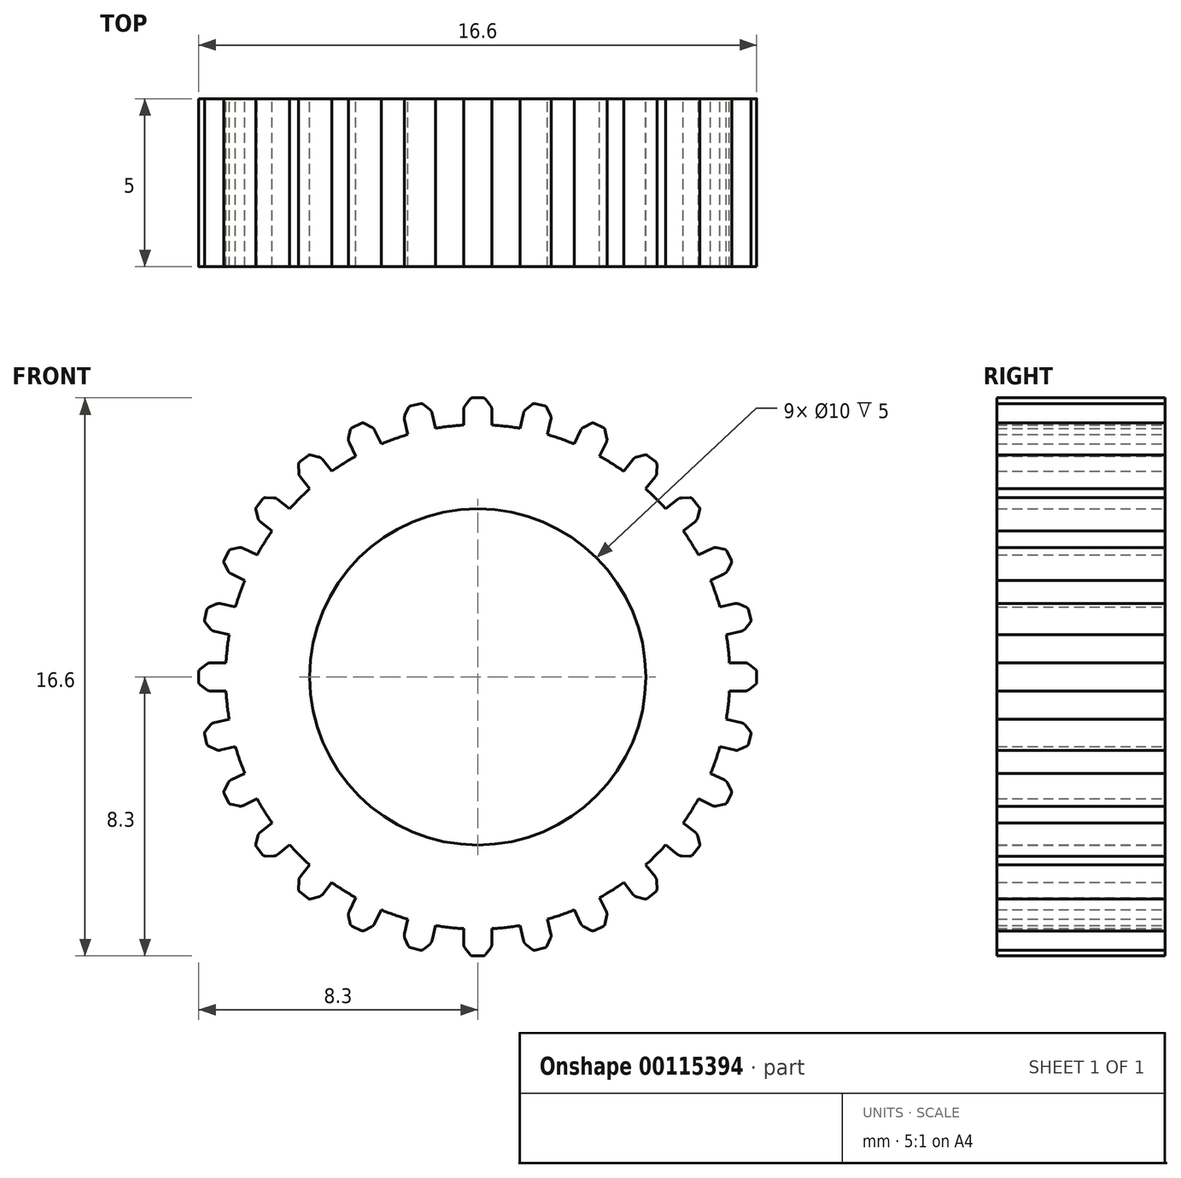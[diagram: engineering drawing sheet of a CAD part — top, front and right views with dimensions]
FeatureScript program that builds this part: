
annotation { "Feature Type Name" : "Feature", "Feature Type Description" : "" }
export const myFeature = defineFeature(function(context is Context, id is Id, definition is map)
    precondition{}
    {
        {
            var Q0;
            Q0=qCreatedBy(makeId("Front.planeOp"),FACE);
            var sketch = newSketch(context, id + "F0", { "sketchPlane" : qUnion([Q0])});
            skCircle(sketch, "E0", {"center": v(0, 0) * mm, "radius": 7.5 * mm});
            skLineSegment(sketch, "E1.bottom", {"start": v(0, 8.3) * mm, "end": v(-0.15, 8.3) * mm});
            skLineSegment(sketch, "E1.left", {"start": v(0, 8.3) * mm, "end": v(0, 7.5) * mm});
            skLineSegment(sketch, "E2.right", {"start": v(-0.42, 7.94) * mm, "end": v(-0.42, 7.49) * mm});
            skLineSegment(sketch, "E3", {"start": v(-0.38, 8.07) * mm, "end": v(-0.23, 8.26) * mm});
            skPoint(sketch, "E4.visualSharp", {"position": v(-0.2, 8.3) * mm});
            skArc(sketch, "E4.filletArc", {"start": v(-0.15, 8.3) * mm, "mid": v(-0.2, 8.29) * mm, "end": v(-0.23, 8.26) * mm});
            skPoint(sketch, "E5.visualSharp", {"position": v(-0.42, 8.01) * mm});
            skArc(sketch, "E5.filletArc", {"start": v(-0.38, 8.07) * mm, "mid": v(-0.4, 8) * mm, "end": v(-0.42, 7.94) * mm});
            skArc(sketch, "E6.MirrorCS", {"start": v(0.15, 8.3) * mm, "mid": v(0.2, 8.29) * mm, "end": v(0.23, 8.26) * mm});
            skArc(sketch, "E7.MirrorCS", {"start": v(0.38, 8.07) * mm, "mid": v(0.4, 8) * mm, "end": v(0.42, 7.94) * mm});
            skLineSegment(sketch, "E8.MirrorCS", {"start": v(0, 8.3) * mm, "end": v(0.15, 8.3) * mm});
            skPoint(sketch, "E9.MirrorP", {"position": v(0.2, 8.3) * mm});
            skLineSegment(sketch, "E10.MirrorCS", {"start": v(0.38, 8.07) * mm, "end": v(0.23, 8.26) * mm});
            skPoint(sketch, "E11.MirrorP", {"position": v(0.42, 8.01) * mm});
            skLineSegment(sketch, "E12.MirrorCS", {"start": v(0.42, 7.94) * mm, "end": v(0.42, 7.49) * mm});
            skPoint(sketch, "E13.1.0", {"position": v(-2.2, 7.72) * mm});
            skPoint(sketch, "E13.1.1", {"position": v(-1.65, 8.14) * mm});
            skPoint(sketch, "E13.1.2", {"position": v(-1.37, 7.9) * mm});
            skPoint(sketch, "E13.1.3", {"position": v(-2.04, 8.05) * mm});
            skArc(sketch, "E13.1.4", {"start": v(-2.16, 7.78) * mm, "mid": v(-2.18, 7.72) * mm, "end": v(-2.18, 7.65) * mm});
            skLineSegment(sketch, "E13.1.5", {"start": v(-1.43, 7.95) * mm, "end": v(-1.61, 8.1) * mm});
            skArc(sketch, "E13.1.6", {"start": v(-1.43, 7.95) * mm, "mid": v(-1.38, 7.9) * mm, "end": v(-1.36, 7.84) * mm});
            skLineSegment(sketch, "E13.1.7", {"start": v(-2.16, 7.78) * mm, "end": v(-2.06, 8) * mm});
            skArc(sketch, "E13.1.8", {"start": v(-1.7, 8.13) * mm, "mid": v(-1.66, 8.13) * mm, "end": v(-1.61, 8.1) * mm});
            skArc(sketch, "E13.1.9", {"start": v(-2, 8.06) * mm, "mid": v(-2.03, 8.04) * mm, "end": v(-2.06, 8) * mm});
            skLineSegment(sketch, "E13.1.10", {"start": v(-1.85, 8.1) * mm, "end": v(-1.7, 8.13) * mm});
            skLineSegment(sketch, "E13.1.11", {"start": v(-1.85, 8.1) * mm, "end": v(-2, 8.06) * mm});
            skLineSegment(sketch, "E13.1.12", {"start": v(-2.18, 7.65) * mm, "end": v(-2.08, 7.2) * mm});
            skLineSegment(sketch, "E13.1.13", {"start": v(-1.36, 7.84) * mm, "end": v(-1.26, 7.4) * mm});
            skPoint(sketch, "E13.2.0", {"position": v(-3.85, 7.04) * mm});
            skPoint(sketch, "E13.2.1", {"position": v(-3.42, 7.56) * mm});
            skPoint(sketch, "E13.2.2", {"position": v(-3.1, 7.4) * mm});
            skPoint(sketch, "E13.2.3", {"position": v(-3.78, 7.4) * mm});
            skArc(sketch, "E13.2.4", {"start": v(-3.84, 7.1) * mm, "mid": v(-3.84, 7.04) * mm, "end": v(-3.83, 6.97) * mm});
            skLineSegment(sketch, "E13.2.5", {"start": v(-3.16, 7.43) * mm, "end": v(-3.38, 7.54) * mm});
            skArc(sketch, "E13.2.6", {"start": v(-3.16, 7.43) * mm, "mid": v(-3.1, 7.4) * mm, "end": v(-3.07, 7.34) * mm});
            skLineSegment(sketch, "E13.2.7", {"start": v(-3.84, 7.1) * mm, "end": v(-3.8, 7.34) * mm});
            skArc(sketch, "E13.2.8", {"start": v(-3.47, 7.54) * mm, "mid": v(-3.42, 7.55) * mm, "end": v(-3.38, 7.54) * mm});
            skArc(sketch, "E13.2.9", {"start": v(-3.74, 7.41) * mm, "mid": v(-3.77, 7.38) * mm, "end": v(-3.8, 7.34) * mm});
            skLineSegment(sketch, "E13.2.10", {"start": v(-3.6, 7.48) * mm, "end": v(-3.47, 7.54) * mm});
            skLineSegment(sketch, "E13.2.11", {"start": v(-3.6, 7.48) * mm, "end": v(-3.74, 7.41) * mm});
            skLineSegment(sketch, "E13.2.12", {"start": v(-3.83, 6.97) * mm, "end": v(-3.63, 6.56) * mm});
            skLineSegment(sketch, "E13.2.13", {"start": v(-3.07, 7.34) * mm, "end": v(-2.87, 6.93) * mm});
            skPoint(sketch, "E13.3.0", {"position": v(-5.32, 6) * mm});
            skPoint(sketch, "E13.3.1", {"position": v(-5.02, 6.61) * mm});
            skPoint(sketch, "E13.3.2", {"position": v(-4.67, 6.53) * mm});
            skPoint(sketch, "E13.3.3", {"position": v(-5.33, 6.36) * mm});
            skArc(sketch, "E13.3.4", {"start": v(-5.33, 6.07) * mm, "mid": v(-5.31, 6) * mm, "end": v(-5.28, 5.95) * mm});
            skLineSegment(sketch, "E13.3.5", {"start": v(-4.73, 6.54) * mm, "end": v(-4.97, 6.6) * mm});
            skArc(sketch, "E13.3.6", {"start": v(-4.73, 6.54) * mm, "mid": v(-4.67, 6.52) * mm, "end": v(-4.62, 6.47) * mm});
            skLineSegment(sketch, "E13.3.7", {"start": v(-5.33, 6.07) * mm, "end": v(-5.33, 6.32) * mm});
            skArc(sketch, "E13.3.8", {"start": v(-5.06, 6.58) * mm, "mid": v(-5.02, 6.6) * mm, "end": v(-4.97, 6.6) * mm});
            skArc(sketch, "E13.3.9", {"start": v(-5.3, 6.4) * mm, "mid": v(-5.32, 6.36) * mm, "end": v(-5.33, 6.32) * mm});
            skLineSegment(sketch, "E13.3.10", {"start": v(-5.17, 6.49) * mm, "end": v(-5.06, 6.58) * mm});
            skLineSegment(sketch, "E13.3.11", {"start": v(-5.17, 6.49) * mm, "end": v(-5.3, 6.4) * mm});
            skLineSegment(sketch, "E13.3.12", {"start": v(-5.28, 5.95) * mm, "end": v(-5, 5.6) * mm});
            skLineSegment(sketch, "E13.3.13", {"start": v(-4.62, 6.47) * mm, "end": v(-4.34, 6.12) * mm});
            skPoint(sketch, "E13.4.0", {"position": v(-6.53, 4.67) * mm});
            skPoint(sketch, "E13.4.1", {"position": v(-6.36, 5.33) * mm});
            skPoint(sketch, "E13.4.2", {"position": v(-6, 5.32) * mm});
            skPoint(sketch, "E13.4.3", {"position": v(-6.61, 5.02) * mm});
            skArc(sketch, "E13.4.4", {"start": v(-6.54, 4.73) * mm, "mid": v(-6.52, 4.67) * mm, "end": v(-6.47, 4.62) * mm});
            skLineSegment(sketch, "E13.4.5", {"start": v(-6.07, 5.33) * mm, "end": v(-6.32, 5.33) * mm});
            skArc(sketch, "E13.4.6", {"start": v(-6.07, 5.33) * mm, "mid": v(-6, 5.31) * mm, "end": v(-5.95, 5.28) * mm});
            skLineSegment(sketch, "E13.4.7", {"start": v(-6.54, 4.73) * mm, "end": v(-6.6, 4.97) * mm});
            skArc(sketch, "E13.4.8", {"start": v(-6.4, 5.3) * mm, "mid": v(-6.36, 5.32) * mm, "end": v(-6.32, 5.33) * mm});
            skArc(sketch, "E13.4.9", {"start": v(-6.58, 5.06) * mm, "mid": v(-6.6, 5.02) * mm, "end": v(-6.6, 4.97) * mm});
            skLineSegment(sketch, "E13.4.10", {"start": v(-6.49, 5.17) * mm, "end": v(-6.4, 5.3) * mm});
            skLineSegment(sketch, "E13.4.11", {"start": v(-6.49, 5.17) * mm, "end": v(-6.58, 5.06) * mm});
            skLineSegment(sketch, "E13.4.12", {"start": v(-6.47, 4.62) * mm, "end": v(-6.12, 4.34) * mm});
            skLineSegment(sketch, "E13.4.13", {"start": v(-5.95, 5.28) * mm, "end": v(-5.6, 5) * mm});
            skPoint(sketch, "E13.5.0", {"position": v(-7.4, 3.1) * mm});
            skPoint(sketch, "E13.5.1", {"position": v(-7.4, 3.78) * mm});
            skPoint(sketch, "E13.5.2", {"position": v(-7.04, 3.85) * mm});
            skPoint(sketch, "E13.5.3", {"position": v(-7.56, 3.42) * mm});
            skArc(sketch, "E13.5.4", {"start": v(-7.43, 3.16) * mm, "mid": v(-7.4, 3.1) * mm, "end": v(-7.34, 3.07) * mm});
            skLineSegment(sketch, "E13.5.5", {"start": v(-7.1, 3.84) * mm, "end": v(-7.34, 3.8) * mm});
            skArc(sketch, "E13.5.6", {"start": v(-7.1, 3.84) * mm, "mid": v(-7.04, 3.84) * mm, "end": v(-6.97, 3.83) * mm});
            skLineSegment(sketch, "E13.5.7", {"start": v(-7.43, 3.16) * mm, "end": v(-7.54, 3.38) * mm});
            skArc(sketch, "E13.5.8", {"start": v(-7.41, 3.74) * mm, "mid": v(-7.38, 3.77) * mm, "end": v(-7.34, 3.8) * mm});
            skArc(sketch, "E13.5.9", {"start": v(-7.54, 3.47) * mm, "mid": v(-7.55, 3.42) * mm, "end": v(-7.54, 3.38) * mm});
            skLineSegment(sketch, "E13.5.10", {"start": v(-7.48, 3.6) * mm, "end": v(-7.41, 3.74) * mm});
            skLineSegment(sketch, "E13.5.11", {"start": v(-7.48, 3.6) * mm, "end": v(-7.54, 3.47) * mm});
            skLineSegment(sketch, "E13.5.12", {"start": v(-7.34, 3.07) * mm, "end": v(-6.93, 2.87) * mm});
            skLineSegment(sketch, "E13.5.13", {"start": v(-6.97, 3.83) * mm, "end": v(-6.56, 3.63) * mm});
            skPoint(sketch, "E13.6.0", {"position": v(-7.9, 1.37) * mm});
            skPoint(sketch, "E13.6.1", {"position": v(-8.05, 2.04) * mm});
            skPoint(sketch, "E13.6.2", {"position": v(-7.72, 2.2) * mm});
            skPoint(sketch, "E13.6.3", {"position": v(-8.14, 1.65) * mm});
            skArc(sketch, "E13.6.4", {"start": v(-7.95, 1.43) * mm, "mid": v(-7.9, 1.38) * mm, "end": v(-7.84, 1.36) * mm});
            skLineSegment(sketch, "E13.6.5", {"start": v(-7.78, 2.16) * mm, "end": v(-8, 2.06) * mm});
            skArc(sketch, "E13.6.6", {"start": v(-7.78, 2.16) * mm, "mid": v(-7.72, 2.18) * mm, "end": v(-7.65, 2.18) * mm});
            skLineSegment(sketch, "E13.6.7", {"start": v(-7.95, 1.43) * mm, "end": v(-8.1, 1.61) * mm});
            skArc(sketch, "E13.6.8", {"start": v(-8.06, 2) * mm, "mid": v(-8.04, 2.03) * mm, "end": v(-8, 2.06) * mm});
            skArc(sketch, "E13.6.9", {"start": v(-8.13, 1.7) * mm, "mid": v(-8.13, 1.66) * mm, "end": v(-8.1, 1.61) * mm});
            skLineSegment(sketch, "E13.6.10", {"start": v(-8.1, 1.85) * mm, "end": v(-8.06, 2) * mm});
            skLineSegment(sketch, "E13.6.11", {"start": v(-8.1, 1.85) * mm, "end": v(-8.13, 1.7) * mm});
            skLineSegment(sketch, "E13.6.12", {"start": v(-7.84, 1.36) * mm, "end": v(-7.4, 1.26) * mm});
            skLineSegment(sketch, "E13.6.13", {"start": v(-7.65, 2.18) * mm, "end": v(-7.2, 2.08) * mm});
            skPoint(sketch, "E13.7.0", {"position": v(-8.01, -0.42) * mm});
            skPoint(sketch, "E13.7.1", {"position": v(-8.3, 0.2) * mm});
            skPoint(sketch, "E13.7.2", {"position": v(-8.01, 0.42) * mm});
            skPoint(sketch, "E13.7.3", {"position": v(-8.3, -0.2) * mm});
            skArc(sketch, "E13.7.4", {"start": v(-8.07, -0.38) * mm, "mid": v(-8, -0.4) * mm, "end": v(-7.94, -0.42) * mm});
            skLineSegment(sketch, "E13.7.5", {"start": v(-8.07, 0.38) * mm, "end": v(-8.26, 0.23) * mm});
            skArc(sketch, "E13.7.6", {"start": v(-8.07, 0.38) * mm, "mid": v(-8, 0.4) * mm, "end": v(-7.94, 0.42) * mm});
            skLineSegment(sketch, "E13.7.7", {"start": v(-8.07, -0.38) * mm, "end": v(-8.26, -0.23) * mm});
            skArc(sketch, "E13.7.8", {"start": v(-8.3, 0.15) * mm, "mid": v(-8.29, 0.2) * mm, "end": v(-8.26, 0.23) * mm});
            skArc(sketch, "E13.7.9", {"start": v(-8.3, -0.15) * mm, "mid": v(-8.29, -0.2) * mm, "end": v(-8.26, -0.23) * mm});
            skLineSegment(sketch, "E13.7.10", {"start": v(-8.3, 0) * mm, "end": v(-8.3, 0.15) * mm});
            skLineSegment(sketch, "E13.7.11", {"start": v(-8.3, 0) * mm, "end": v(-8.3, -0.15) * mm});
            skLineSegment(sketch, "E13.7.12", {"start": v(-7.94, -0.42) * mm, "end": v(-7.49, -0.42) * mm});
            skLineSegment(sketch, "E13.7.13", {"start": v(-7.94, 0.42) * mm, "end": v(-7.49, 0.42) * mm});
            skPoint(sketch, "E13.8.0", {"position": v(-7.72, -2.2) * mm});
            skPoint(sketch, "E13.8.1", {"position": v(-8.14, -1.65) * mm});
            skPoint(sketch, "E13.8.2", {"position": v(-7.9, -1.37) * mm});
            skPoint(sketch, "E13.8.3", {"position": v(-8.05, -2.04) * mm});
            skArc(sketch, "E13.8.4", {"start": v(-7.78, -2.16) * mm, "mid": v(-7.72, -2.18) * mm, "end": v(-7.65, -2.18) * mm});
            skLineSegment(sketch, "E13.8.5", {"start": v(-7.95, -1.43) * mm, "end": v(-8.1, -1.61) * mm});
            skArc(sketch, "E13.8.6", {"start": v(-7.95, -1.43) * mm, "mid": v(-7.9, -1.38) * mm, "end": v(-7.84, -1.36) * mm});
            skLineSegment(sketch, "E13.8.7", {"start": v(-7.78, -2.16) * mm, "end": v(-8, -2.06) * mm});
            skArc(sketch, "E13.8.8", {"start": v(-8.13, -1.7) * mm, "mid": v(-8.13, -1.66) * mm, "end": v(-8.1, -1.61) * mm});
            skArc(sketch, "E13.8.9", {"start": v(-8.06, -2) * mm, "mid": v(-8.04, -2.03) * mm, "end": v(-8, -2.06) * mm});
            skLineSegment(sketch, "E13.8.10", {"start": v(-8.1, -1.85) * mm, "end": v(-8.13, -1.7) * mm});
            skLineSegment(sketch, "E13.8.11", {"start": v(-8.1, -1.85) * mm, "end": v(-8.06, -2) * mm});
            skLineSegment(sketch, "E13.8.12", {"start": v(-7.65, -2.18) * mm, "end": v(-7.2, -2.08) * mm});
            skLineSegment(sketch, "E13.8.13", {"start": v(-7.84, -1.36) * mm, "end": v(-7.4, -1.26) * mm});
            skPoint(sketch, "E13.9.0", {"position": v(-7.04, -3.85) * mm});
            skPoint(sketch, "E13.9.1", {"position": v(-7.56, -3.42) * mm});
            skPoint(sketch, "E13.9.2", {"position": v(-7.4, -3.1) * mm});
            skPoint(sketch, "E13.9.3", {"position": v(-7.4, -3.78) * mm});
            skArc(sketch, "E13.9.4", {"start": v(-7.1, -3.84) * mm, "mid": v(-7.04, -3.84) * mm, "end": v(-6.97, -3.83) * mm});
            skLineSegment(sketch, "E13.9.5", {"start": v(-7.43, -3.16) * mm, "end": v(-7.54, -3.38) * mm});
            skArc(sketch, "E13.9.6", {"start": v(-7.43, -3.16) * mm, "mid": v(-7.4, -3.1) * mm, "end": v(-7.34, -3.07) * mm});
            skLineSegment(sketch, "E13.9.7", {"start": v(-7.1, -3.84) * mm, "end": v(-7.34, -3.8) * mm});
            skArc(sketch, "E13.9.8", {"start": v(-7.54, -3.47) * mm, "mid": v(-7.55, -3.42) * mm, "end": v(-7.54, -3.38) * mm});
            skArc(sketch, "E13.9.9", {"start": v(-7.41, -3.74) * mm, "mid": v(-7.38, -3.77) * mm, "end": v(-7.34, -3.8) * mm});
            skLineSegment(sketch, "E13.9.10", {"start": v(-7.48, -3.6) * mm, "end": v(-7.54, -3.47) * mm});
            skLineSegment(sketch, "E13.9.11", {"start": v(-7.48, -3.6) * mm, "end": v(-7.41, -3.74) * mm});
            skLineSegment(sketch, "E13.9.12", {"start": v(-6.97, -3.83) * mm, "end": v(-6.56, -3.63) * mm});
            skLineSegment(sketch, "E13.9.13", {"start": v(-7.34, -3.07) * mm, "end": v(-6.93, -2.87) * mm});
            skPoint(sketch, "E13.10.0", {"position": v(-6, -5.32) * mm});
            skPoint(sketch, "E13.10.1", {"position": v(-6.61, -5.02) * mm});
            skPoint(sketch, "E13.10.2", {"position": v(-6.53, -4.67) * mm});
            skPoint(sketch, "E13.10.3", {"position": v(-6.36, -5.33) * mm});
            skArc(sketch, "E13.10.4", {"start": v(-6.07, -5.33) * mm, "mid": v(-6, -5.31) * mm, "end": v(-5.95, -5.28) * mm});
            skLineSegment(sketch, "E13.10.5", {"start": v(-6.54, -4.73) * mm, "end": v(-6.6, -4.97) * mm});
            skArc(sketch, "E13.10.6", {"start": v(-6.54, -4.73) * mm, "mid": v(-6.52, -4.67) * mm, "end": v(-6.47, -4.62) * mm});
            skLineSegment(sketch, "E13.10.7", {"start": v(-6.07, -5.33) * mm, "end": v(-6.32, -5.33) * mm});
            skArc(sketch, "E13.10.8", {"start": v(-6.58, -5.06) * mm, "mid": v(-6.6, -5.02) * mm, "end": v(-6.6, -4.97) * mm});
            skArc(sketch, "E13.10.9", {"start": v(-6.4, -5.3) * mm, "mid": v(-6.36, -5.32) * mm, "end": v(-6.32, -5.33) * mm});
            skLineSegment(sketch, "E13.10.10", {"start": v(-6.49, -5.17) * mm, "end": v(-6.58, -5.06) * mm});
            skLineSegment(sketch, "E13.10.11", {"start": v(-6.49, -5.17) * mm, "end": v(-6.4, -5.3) * mm});
            skLineSegment(sketch, "E13.10.12", {"start": v(-5.95, -5.28) * mm, "end": v(-5.6, -5) * mm});
            skLineSegment(sketch, "E13.10.13", {"start": v(-6.47, -4.62) * mm, "end": v(-6.12, -4.34) * mm});
            skPoint(sketch, "E13.11.0", {"position": v(-4.67, -6.53) * mm});
            skPoint(sketch, "E13.11.1", {"position": v(-5.33, -6.36) * mm});
            skPoint(sketch, "E13.11.2", {"position": v(-5.32, -6) * mm});
            skPoint(sketch, "E13.11.3", {"position": v(-5.02, -6.61) * mm});
            skArc(sketch, "E13.11.4", {"start": v(-4.73, -6.54) * mm, "mid": v(-4.67, -6.52) * mm, "end": v(-4.62, -6.47) * mm});
            skLineSegment(sketch, "E13.11.5", {"start": v(-5.33, -6.07) * mm, "end": v(-5.33, -6.32) * mm});
            skArc(sketch, "E13.11.6", {"start": v(-5.33, -6.07) * mm, "mid": v(-5.31, -6) * mm, "end": v(-5.28, -5.95) * mm});
            skLineSegment(sketch, "E13.11.7", {"start": v(-4.73, -6.54) * mm, "end": v(-4.97, -6.6) * mm});
            skArc(sketch, "E13.11.8", {"start": v(-5.3, -6.4) * mm, "mid": v(-5.32, -6.36) * mm, "end": v(-5.33, -6.32) * mm});
            skArc(sketch, "E13.11.9", {"start": v(-5.06, -6.58) * mm, "mid": v(-5.02, -6.6) * mm, "end": v(-4.97, -6.6) * mm});
            skLineSegment(sketch, "E13.11.10", {"start": v(-5.17, -6.49) * mm, "end": v(-5.3, -6.4) * mm});
            skLineSegment(sketch, "E13.11.11", {"start": v(-5.17, -6.49) * mm, "end": v(-5.06, -6.58) * mm});
            skLineSegment(sketch, "E13.11.12", {"start": v(-4.62, -6.47) * mm, "end": v(-4.34, -6.12) * mm});
            skLineSegment(sketch, "E13.11.13", {"start": v(-5.28, -5.95) * mm, "end": v(-5, -5.6) * mm});
            skPoint(sketch, "E13.12.0", {"position": v(-3.1, -7.4) * mm});
            skPoint(sketch, "E13.12.1", {"position": v(-3.78, -7.4) * mm});
            skPoint(sketch, "E13.12.2", {"position": v(-3.85, -7.04) * mm});
            skPoint(sketch, "E13.12.3", {"position": v(-3.42, -7.56) * mm});
            skArc(sketch, "E13.12.4", {"start": v(-3.16, -7.43) * mm, "mid": v(-3.1, -7.4) * mm, "end": v(-3.07, -7.34) * mm});
            skLineSegment(sketch, "E13.12.5", {"start": v(-3.84, -7.1) * mm, "end": v(-3.8, -7.34) * mm});
            skArc(sketch, "E13.12.6", {"start": v(-3.84, -7.1) * mm, "mid": v(-3.84, -7.04) * mm, "end": v(-3.83, -6.97) * mm});
            skLineSegment(sketch, "E13.12.7", {"start": v(-3.16, -7.43) * mm, "end": v(-3.38, -7.54) * mm});
            skArc(sketch, "E13.12.8", {"start": v(-3.74, -7.41) * mm, "mid": v(-3.77, -7.38) * mm, "end": v(-3.8, -7.34) * mm});
            skArc(sketch, "E13.12.9", {"start": v(-3.47, -7.54) * mm, "mid": v(-3.42, -7.55) * mm, "end": v(-3.38, -7.54) * mm});
            skLineSegment(sketch, "E13.12.10", {"start": v(-3.6, -7.48) * mm, "end": v(-3.74, -7.41) * mm});
            skLineSegment(sketch, "E13.12.11", {"start": v(-3.6, -7.48) * mm, "end": v(-3.47, -7.54) * mm});
            skLineSegment(sketch, "E13.12.12", {"start": v(-3.07, -7.34) * mm, "end": v(-2.87, -6.93) * mm});
            skLineSegment(sketch, "E13.12.13", {"start": v(-3.83, -6.97) * mm, "end": v(-3.63, -6.56) * mm});
            skPoint(sketch, "E13.13.0", {"position": v(-1.37, -7.9) * mm});
            skPoint(sketch, "E13.13.1", {"position": v(-2.04, -8.05) * mm});
            skPoint(sketch, "E13.13.2", {"position": v(-2.2, -7.72) * mm});
            skPoint(sketch, "E13.13.3", {"position": v(-1.65, -8.14) * mm});
            skArc(sketch, "E13.13.4", {"start": v(-1.43, -7.95) * mm, "mid": v(-1.38, -7.9) * mm, "end": v(-1.36, -7.84) * mm});
            skLineSegment(sketch, "E13.13.5", {"start": v(-2.16, -7.78) * mm, "end": v(-2.06, -8) * mm});
            skArc(sketch, "E13.13.6", {"start": v(-2.16, -7.78) * mm, "mid": v(-2.18, -7.72) * mm, "end": v(-2.18, -7.65) * mm});
            skLineSegment(sketch, "E13.13.7", {"start": v(-1.43, -7.95) * mm, "end": v(-1.61, -8.1) * mm});
            skArc(sketch, "E13.13.8", {"start": v(-2, -8.06) * mm, "mid": v(-2.03, -8.04) * mm, "end": v(-2.06, -8) * mm});
            skArc(sketch, "E13.13.9", {"start": v(-1.7, -8.13) * mm, "mid": v(-1.66, -8.13) * mm, "end": v(-1.61, -8.1) * mm});
            skLineSegment(sketch, "E13.13.10", {"start": v(-1.85, -8.1) * mm, "end": v(-2, -8.06) * mm});
            skLineSegment(sketch, "E13.13.11", {"start": v(-1.85, -8.1) * mm, "end": v(-1.7, -8.13) * mm});
            skLineSegment(sketch, "E13.13.12", {"start": v(-1.36, -7.84) * mm, "end": v(-1.26, -7.4) * mm});
            skLineSegment(sketch, "E13.13.13", {"start": v(-2.18, -7.65) * mm, "end": v(-2.08, -7.2) * mm});
            skPoint(sketch, "E13.14.0", {"position": v(0.42, -8.01) * mm});
            skPoint(sketch, "E13.14.1", {"position": v(-0.2, -8.3) * mm});
            skPoint(sketch, "E13.14.2", {"position": v(-0.42, -8.01) * mm});
            skPoint(sketch, "E13.14.3", {"position": v(0.2, -8.3) * mm});
            skArc(sketch, "E13.14.4", {"start": v(0.38, -8.07) * mm, "mid": v(0.4, -8) * mm, "end": v(0.42, -7.94) * mm});
            skLineSegment(sketch, "E13.14.5", {"start": v(-0.38, -8.07) * mm, "end": v(-0.23, -8.26) * mm});
            skArc(sketch, "E13.14.6", {"start": v(-0.38, -8.07) * mm, "mid": v(-0.4, -8) * mm, "end": v(-0.42, -7.94) * mm});
            skLineSegment(sketch, "E13.14.7", {"start": v(0.38, -8.07) * mm, "end": v(0.23, -8.26) * mm});
            skArc(sketch, "E13.14.8", {"start": v(-0.15, -8.3) * mm, "mid": v(-0.2, -8.29) * mm, "end": v(-0.23, -8.26) * mm});
            skArc(sketch, "E13.14.9", {"start": v(0.15, -8.3) * mm, "mid": v(0.2, -8.29) * mm, "end": v(0.23, -8.26) * mm});
            skLineSegment(sketch, "E13.14.10", {"start": v(0, -8.3) * mm, "end": v(-0.15, -8.3) * mm});
            skLineSegment(sketch, "E13.14.11", {"start": v(0, -8.3) * mm, "end": v(0.15, -8.3) * mm});
            skLineSegment(sketch, "E13.14.12", {"start": v(0.42, -7.94) * mm, "end": v(0.42, -7.49) * mm});
            skLineSegment(sketch, "E13.14.13", {"start": v(-0.42, -7.94) * mm, "end": v(-0.42, -7.49) * mm});
            skPoint(sketch, "E13.15.0", {"position": v(2.2, -7.72) * mm});
            skPoint(sketch, "E13.15.1", {"position": v(1.65, -8.14) * mm});
            skPoint(sketch, "E13.15.2", {"position": v(1.37, -7.9) * mm});
            skPoint(sketch, "E13.15.3", {"position": v(2.04, -8.05) * mm});
            skArc(sketch, "E13.15.4", {"start": v(2.16, -7.78) * mm, "mid": v(2.18, -7.72) * mm, "end": v(2.18, -7.65) * mm});
            skLineSegment(sketch, "E13.15.5", {"start": v(1.43, -7.95) * mm, "end": v(1.61, -8.1) * mm});
            skArc(sketch, "E13.15.6", {"start": v(1.43, -7.95) * mm, "mid": v(1.38, -7.9) * mm, "end": v(1.36, -7.84) * mm});
            skLineSegment(sketch, "E13.15.7", {"start": v(2.16, -7.78) * mm, "end": v(2.06, -8) * mm});
            skArc(sketch, "E13.15.8", {"start": v(1.7, -8.13) * mm, "mid": v(1.66, -8.13) * mm, "end": v(1.61, -8.1) * mm});
            skArc(sketch, "E13.15.9", {"start": v(2, -8.06) * mm, "mid": v(2.03, -8.04) * mm, "end": v(2.06, -8) * mm});
            skLineSegment(sketch, "E13.15.10", {"start": v(1.85, -8.1) * mm, "end": v(1.7, -8.13) * mm});
            skLineSegment(sketch, "E13.15.11", {"start": v(1.85, -8.1) * mm, "end": v(2, -8.06) * mm});
            skLineSegment(sketch, "E13.15.12", {"start": v(2.18, -7.65) * mm, "end": v(2.08, -7.2) * mm});
            skLineSegment(sketch, "E13.15.13", {"start": v(1.36, -7.84) * mm, "end": v(1.26, -7.4) * mm});
            skPoint(sketch, "E13.16.0", {"position": v(3.85, -7.04) * mm});
            skPoint(sketch, "E13.16.1", {"position": v(3.42, -7.56) * mm});
            skPoint(sketch, "E13.16.2", {"position": v(3.1, -7.4) * mm});
            skPoint(sketch, "E13.16.3", {"position": v(3.78, -7.4) * mm});
            skArc(sketch, "E13.16.4", {"start": v(3.84, -7.1) * mm, "mid": v(3.84, -7.04) * mm, "end": v(3.83, -6.97) * mm});
            skLineSegment(sketch, "E13.16.5", {"start": v(3.16, -7.43) * mm, "end": v(3.38, -7.54) * mm});
            skArc(sketch, "E13.16.6", {"start": v(3.16, -7.43) * mm, "mid": v(3.1, -7.4) * mm, "end": v(3.07, -7.34) * mm});
            skLineSegment(sketch, "E13.16.7", {"start": v(3.84, -7.1) * mm, "end": v(3.8, -7.34) * mm});
            skArc(sketch, "E13.16.8", {"start": v(3.47, -7.54) * mm, "mid": v(3.42, -7.55) * mm, "end": v(3.38, -7.54) * mm});
            skArc(sketch, "E13.16.9", {"start": v(3.74, -7.41) * mm, "mid": v(3.77, -7.38) * mm, "end": v(3.8, -7.34) * mm});
            skLineSegment(sketch, "E13.16.10", {"start": v(3.6, -7.48) * mm, "end": v(3.47, -7.54) * mm});
            skLineSegment(sketch, "E13.16.11", {"start": v(3.6, -7.48) * mm, "end": v(3.74, -7.41) * mm});
            skLineSegment(sketch, "E13.16.12", {"start": v(3.83, -6.97) * mm, "end": v(3.63, -6.56) * mm});
            skLineSegment(sketch, "E13.16.13", {"start": v(3.07, -7.34) * mm, "end": v(2.87, -6.93) * mm});
            skPoint(sketch, "E13.17.0", {"position": v(5.32, -6) * mm});
            skPoint(sketch, "E13.17.1", {"position": v(5.02, -6.61) * mm});
            skPoint(sketch, "E13.17.2", {"position": v(4.67, -6.53) * mm});
            skPoint(sketch, "E13.17.3", {"position": v(5.33, -6.36) * mm});
            skArc(sketch, "E13.17.4", {"start": v(5.33, -6.07) * mm, "mid": v(5.31, -6) * mm, "end": v(5.28, -5.95) * mm});
            skLineSegment(sketch, "E13.17.5", {"start": v(4.73, -6.54) * mm, "end": v(4.97, -6.6) * mm});
            skArc(sketch, "E13.17.6", {"start": v(4.73, -6.54) * mm, "mid": v(4.67, -6.52) * mm, "end": v(4.62, -6.47) * mm});
            skLineSegment(sketch, "E13.17.7", {"start": v(5.33, -6.07) * mm, "end": v(5.33, -6.32) * mm});
            skArc(sketch, "E13.17.8", {"start": v(5.06, -6.58) * mm, "mid": v(5.02, -6.6) * mm, "end": v(4.97, -6.6) * mm});
            skArc(sketch, "E13.17.9", {"start": v(5.3, -6.4) * mm, "mid": v(5.32, -6.36) * mm, "end": v(5.33, -6.32) * mm});
            skLineSegment(sketch, "E13.17.10", {"start": v(5.17, -6.49) * mm, "end": v(5.06, -6.58) * mm});
            skLineSegment(sketch, "E13.17.11", {"start": v(5.17, -6.49) * mm, "end": v(5.3, -6.4) * mm});
            skLineSegment(sketch, "E13.17.12", {"start": v(5.28, -5.95) * mm, "end": v(5, -5.6) * mm});
            skLineSegment(sketch, "E13.17.13", {"start": v(4.62, -6.47) * mm, "end": v(4.34, -6.12) * mm});
            skPoint(sketch, "E13.18.0", {"position": v(6.53, -4.67) * mm});
            skPoint(sketch, "E13.18.1", {"position": v(6.36, -5.33) * mm});
            skPoint(sketch, "E13.18.2", {"position": v(6, -5.32) * mm});
            skPoint(sketch, "E13.18.3", {"position": v(6.61, -5.02) * mm});
            skArc(sketch, "E13.18.4", {"start": v(6.54, -4.73) * mm, "mid": v(6.52, -4.67) * mm, "end": v(6.47, -4.62) * mm});
            skLineSegment(sketch, "E13.18.5", {"start": v(6.07, -5.33) * mm, "end": v(6.32, -5.33) * mm});
            skArc(sketch, "E13.18.6", {"start": v(6.07, -5.33) * mm, "mid": v(6, -5.31) * mm, "end": v(5.95, -5.28) * mm});
            skLineSegment(sketch, "E13.18.7", {"start": v(6.54, -4.73) * mm, "end": v(6.6, -4.97) * mm});
            skArc(sketch, "E13.18.8", {"start": v(6.4, -5.3) * mm, "mid": v(6.36, -5.32) * mm, "end": v(6.32, -5.33) * mm});
            skArc(sketch, "E13.18.9", {"start": v(6.58, -5.06) * mm, "mid": v(6.6, -5.02) * mm, "end": v(6.6, -4.97) * mm});
            skLineSegment(sketch, "E13.18.10", {"start": v(6.49, -5.17) * mm, "end": v(6.4, -5.3) * mm});
            skLineSegment(sketch, "E13.18.11", {"start": v(6.49, -5.17) * mm, "end": v(6.58, -5.06) * mm});
            skLineSegment(sketch, "E13.18.12", {"start": v(6.47, -4.62) * mm, "end": v(6.12, -4.34) * mm});
            skLineSegment(sketch, "E13.18.13", {"start": v(5.95, -5.28) * mm, "end": v(5.6, -5) * mm});
            skPoint(sketch, "E13.19.0", {"position": v(7.4, -3.1) * mm});
            skPoint(sketch, "E13.19.1", {"position": v(7.4, -3.78) * mm});
            skPoint(sketch, "E13.19.2", {"position": v(7.04, -3.85) * mm});
            skPoint(sketch, "E13.19.3", {"position": v(7.56, -3.42) * mm});
            skArc(sketch, "E13.19.4", {"start": v(7.43, -3.16) * mm, "mid": v(7.4, -3.1) * mm, "end": v(7.34, -3.07) * mm});
            skLineSegment(sketch, "E13.19.5", {"start": v(7.1, -3.84) * mm, "end": v(7.34, -3.8) * mm});
            skArc(sketch, "E13.19.6", {"start": v(7.1, -3.84) * mm, "mid": v(7.04, -3.84) * mm, "end": v(6.97, -3.83) * mm});
            skLineSegment(sketch, "E13.19.7", {"start": v(7.43, -3.16) * mm, "end": v(7.54, -3.38) * mm});
            skArc(sketch, "E13.19.8", {"start": v(7.41, -3.74) * mm, "mid": v(7.38, -3.77) * mm, "end": v(7.34, -3.8) * mm});
            skArc(sketch, "E13.19.9", {"start": v(7.54, -3.47) * mm, "mid": v(7.55, -3.42) * mm, "end": v(7.54, -3.38) * mm});
            skLineSegment(sketch, "E13.19.10", {"start": v(7.48, -3.6) * mm, "end": v(7.41, -3.74) * mm});
            skLineSegment(sketch, "E13.19.11", {"start": v(7.48, -3.6) * mm, "end": v(7.54, -3.47) * mm});
            skLineSegment(sketch, "E13.19.12", {"start": v(7.34, -3.07) * mm, "end": v(6.93, -2.87) * mm});
            skLineSegment(sketch, "E13.19.13", {"start": v(6.97, -3.83) * mm, "end": v(6.56, -3.63) * mm});
            skPoint(sketch, "E13.20.0", {"position": v(7.9, -1.37) * mm});
            skPoint(sketch, "E13.20.1", {"position": v(8.05, -2.04) * mm});
            skPoint(sketch, "E13.20.2", {"position": v(7.72, -2.2) * mm});
            skPoint(sketch, "E13.20.3", {"position": v(8.14, -1.65) * mm});
            skArc(sketch, "E13.20.4", {"start": v(7.95, -1.43) * mm, "mid": v(7.9, -1.38) * mm, "end": v(7.84, -1.36) * mm});
            skLineSegment(sketch, "E13.20.5", {"start": v(7.78, -2.16) * mm, "end": v(8, -2.06) * mm});
            skArc(sketch, "E13.20.6", {"start": v(7.78, -2.16) * mm, "mid": v(7.72, -2.18) * mm, "end": v(7.65, -2.18) * mm});
            skLineSegment(sketch, "E13.20.7", {"start": v(7.95, -1.43) * mm, "end": v(8.1, -1.61) * mm});
            skArc(sketch, "E13.20.8", {"start": v(8.06, -2) * mm, "mid": v(8.04, -2.03) * mm, "end": v(8, -2.06) * mm});
            skArc(sketch, "E13.20.9", {"start": v(8.13, -1.7) * mm, "mid": v(8.13, -1.66) * mm, "end": v(8.1, -1.61) * mm});
            skLineSegment(sketch, "E13.20.10", {"start": v(8.1, -1.85) * mm, "end": v(8.06, -2) * mm});
            skLineSegment(sketch, "E13.20.11", {"start": v(8.1, -1.85) * mm, "end": v(8.13, -1.7) * mm});
            skLineSegment(sketch, "E13.20.12", {"start": v(7.84, -1.36) * mm, "end": v(7.4, -1.26) * mm});
            skLineSegment(sketch, "E13.20.13", {"start": v(7.65, -2.18) * mm, "end": v(7.2, -2.08) * mm});
            skPoint(sketch, "E13.21.0", {"position": v(8.01, 0.42) * mm});
            skPoint(sketch, "E13.21.1", {"position": v(8.3, -0.2) * mm});
            skPoint(sketch, "E13.21.2", {"position": v(8.01, -0.42) * mm});
            skPoint(sketch, "E13.21.3", {"position": v(8.3, 0.2) * mm});
            skArc(sketch, "E13.21.4", {"start": v(8.07, 0.38) * mm, "mid": v(8, 0.4) * mm, "end": v(7.94, 0.42) * mm});
            skLineSegment(sketch, "E13.21.5", {"start": v(8.07, -0.38) * mm, "end": v(8.26, -0.23) * mm});
            skArc(sketch, "E13.21.6", {"start": v(8.07, -0.38) * mm, "mid": v(8, -0.4) * mm, "end": v(7.94, -0.42) * mm});
            skLineSegment(sketch, "E13.21.7", {"start": v(8.07, 0.38) * mm, "end": v(8.26, 0.23) * mm});
            skArc(sketch, "E13.21.8", {"start": v(8.3, -0.15) * mm, "mid": v(8.29, -0.2) * mm, "end": v(8.26, -0.23) * mm});
            skArc(sketch, "E13.21.9", {"start": v(8.3, 0.15) * mm, "mid": v(8.29, 0.2) * mm, "end": v(8.26, 0.23) * mm});
            skLineSegment(sketch, "E13.21.10", {"start": v(8.3, 0) * mm, "end": v(8.3, -0.15) * mm});
            skLineSegment(sketch, "E13.21.11", {"start": v(8.3, 0) * mm, "end": v(8.3, 0.15) * mm});
            skLineSegment(sketch, "E13.21.12", {"start": v(7.94, 0.42) * mm, "end": v(7.49, 0.42) * mm});
            skLineSegment(sketch, "E13.21.13", {"start": v(7.94, -0.42) * mm, "end": v(7.49, -0.42) * mm});
            skPoint(sketch, "E13.22.0", {"position": v(7.72, 2.2) * mm});
            skPoint(sketch, "E13.22.1", {"position": v(8.14, 1.65) * mm});
            skPoint(sketch, "E13.22.2", {"position": v(7.9, 1.37) * mm});
            skPoint(sketch, "E13.22.3", {"position": v(8.05, 2.04) * mm});
            skArc(sketch, "E13.22.4", {"start": v(7.78, 2.16) * mm, "mid": v(7.72, 2.18) * mm, "end": v(7.65, 2.18) * mm});
            skLineSegment(sketch, "E13.22.5", {"start": v(7.95, 1.43) * mm, "end": v(8.1, 1.61) * mm});
            skArc(sketch, "E13.22.6", {"start": v(7.95, 1.43) * mm, "mid": v(7.9, 1.38) * mm, "end": v(7.84, 1.36) * mm});
            skLineSegment(sketch, "E13.22.7", {"start": v(7.78, 2.16) * mm, "end": v(8, 2.06) * mm});
            skArc(sketch, "E13.22.8", {"start": v(8.13, 1.7) * mm, "mid": v(8.13, 1.66) * mm, "end": v(8.1, 1.61) * mm});
            skArc(sketch, "E13.22.9", {"start": v(8.06, 2) * mm, "mid": v(8.04, 2.03) * mm, "end": v(8, 2.06) * mm});
            skLineSegment(sketch, "E13.22.10", {"start": v(8.1, 1.85) * mm, "end": v(8.13, 1.7) * mm});
            skLineSegment(sketch, "E13.22.11", {"start": v(8.1, 1.85) * mm, "end": v(8.06, 2) * mm});
            skLineSegment(sketch, "E13.22.12", {"start": v(7.65, 2.18) * mm, "end": v(7.2, 2.08) * mm});
            skLineSegment(sketch, "E13.22.13", {"start": v(7.84, 1.36) * mm, "end": v(7.4, 1.26) * mm});
            skPoint(sketch, "E13.23.0", {"position": v(7.04, 3.85) * mm});
            skPoint(sketch, "E13.23.1", {"position": v(7.56, 3.42) * mm});
            skPoint(sketch, "E13.23.2", {"position": v(7.4, 3.1) * mm});
            skPoint(sketch, "E13.23.3", {"position": v(7.4, 3.78) * mm});
            skArc(sketch, "E13.23.4", {"start": v(7.1, 3.84) * mm, "mid": v(7.04, 3.84) * mm, "end": v(6.97, 3.83) * mm});
            skLineSegment(sketch, "E13.23.5", {"start": v(7.43, 3.16) * mm, "end": v(7.54, 3.38) * mm});
            skArc(sketch, "E13.23.6", {"start": v(7.43, 3.16) * mm, "mid": v(7.4, 3.1) * mm, "end": v(7.34, 3.07) * mm});
            skLineSegment(sketch, "E13.23.7", {"start": v(7.1, 3.84) * mm, "end": v(7.34, 3.8) * mm});
            skArc(sketch, "E13.23.8", {"start": v(7.54, 3.47) * mm, "mid": v(7.55, 3.42) * mm, "end": v(7.54, 3.38) * mm});
            skArc(sketch, "E13.23.9", {"start": v(7.41, 3.74) * mm, "mid": v(7.38, 3.77) * mm, "end": v(7.34, 3.8) * mm});
            skLineSegment(sketch, "E13.23.10", {"start": v(7.48, 3.6) * mm, "end": v(7.54, 3.47) * mm});
            skLineSegment(sketch, "E13.23.11", {"start": v(7.48, 3.6) * mm, "end": v(7.41, 3.74) * mm});
            skLineSegment(sketch, "E13.23.12", {"start": v(6.97, 3.83) * mm, "end": v(6.56, 3.63) * mm});
            skLineSegment(sketch, "E13.23.13", {"start": v(7.34, 3.07) * mm, "end": v(6.93, 2.87) * mm});
            skPoint(sketch, "E13.24.0", {"position": v(6, 5.32) * mm});
            skPoint(sketch, "E13.24.1", {"position": v(6.61, 5.02) * mm});
            skPoint(sketch, "E13.24.2", {"position": v(6.53, 4.67) * mm});
            skPoint(sketch, "E13.24.3", {"position": v(6.36, 5.33) * mm});
            skArc(sketch, "E13.24.4", {"start": v(6.07, 5.33) * mm, "mid": v(6, 5.31) * mm, "end": v(5.95, 5.28) * mm});
            skLineSegment(sketch, "E13.24.5", {"start": v(6.54, 4.73) * mm, "end": v(6.6, 4.97) * mm});
            skArc(sketch, "E13.24.6", {"start": v(6.54, 4.73) * mm, "mid": v(6.52, 4.67) * mm, "end": v(6.47, 4.62) * mm});
            skLineSegment(sketch, "E13.24.7", {"start": v(6.07, 5.33) * mm, "end": v(6.32, 5.33) * mm});
            skArc(sketch, "E13.24.8", {"start": v(6.58, 5.06) * mm, "mid": v(6.6, 5.02) * mm, "end": v(6.6, 4.97) * mm});
            skArc(sketch, "E13.24.9", {"start": v(6.4, 5.3) * mm, "mid": v(6.36, 5.32) * mm, "end": v(6.32, 5.33) * mm});
            skLineSegment(sketch, "E13.24.10", {"start": v(6.49, 5.17) * mm, "end": v(6.58, 5.06) * mm});
            skLineSegment(sketch, "E13.24.11", {"start": v(6.49, 5.17) * mm, "end": v(6.4, 5.3) * mm});
            skLineSegment(sketch, "E13.24.12", {"start": v(5.95, 5.28) * mm, "end": v(5.6, 5) * mm});
            skLineSegment(sketch, "E13.24.13", {"start": v(6.47, 4.62) * mm, "end": v(6.12, 4.34) * mm});
            skPoint(sketch, "E13.25.0", {"position": v(4.67, 6.53) * mm});
            skPoint(sketch, "E13.25.1", {"position": v(5.33, 6.36) * mm});
            skPoint(sketch, "E13.25.2", {"position": v(5.32, 6) * mm});
            skPoint(sketch, "E13.25.3", {"position": v(5.02, 6.61) * mm});
            skArc(sketch, "E13.25.4", {"start": v(4.73, 6.54) * mm, "mid": v(4.67, 6.52) * mm, "end": v(4.62, 6.47) * mm});
            skLineSegment(sketch, "E13.25.5", {"start": v(5.33, 6.07) * mm, "end": v(5.33, 6.32) * mm});
            skArc(sketch, "E13.25.6", {"start": v(5.33, 6.07) * mm, "mid": v(5.31, 6) * mm, "end": v(5.28, 5.95) * mm});
            skLineSegment(sketch, "E13.25.7", {"start": v(4.73, 6.54) * mm, "end": v(4.97, 6.6) * mm});
            skArc(sketch, "E13.25.8", {"start": v(5.3, 6.4) * mm, "mid": v(5.32, 6.36) * mm, "end": v(5.33, 6.32) * mm});
            skArc(sketch, "E13.25.9", {"start": v(5.06, 6.58) * mm, "mid": v(5.02, 6.6) * mm, "end": v(4.97, 6.6) * mm});
            skLineSegment(sketch, "E13.25.10", {"start": v(5.17, 6.49) * mm, "end": v(5.3, 6.4) * mm});
            skLineSegment(sketch, "E13.25.11", {"start": v(5.17, 6.49) * mm, "end": v(5.06, 6.58) * mm});
            skLineSegment(sketch, "E13.25.12", {"start": v(4.62, 6.47) * mm, "end": v(4.34, 6.12) * mm});
            skLineSegment(sketch, "E13.25.13", {"start": v(5.28, 5.95) * mm, "end": v(5, 5.6) * mm});
            skPoint(sketch, "E13.26.0", {"position": v(3.1, 7.4) * mm});
            skPoint(sketch, "E13.26.1", {"position": v(3.78, 7.4) * mm});
            skPoint(sketch, "E13.26.2", {"position": v(3.85, 7.04) * mm});
            skPoint(sketch, "E13.26.3", {"position": v(3.42, 7.56) * mm});
            skArc(sketch, "E13.26.4", {"start": v(3.16, 7.43) * mm, "mid": v(3.1, 7.4) * mm, "end": v(3.07, 7.34) * mm});
            skLineSegment(sketch, "E13.26.5", {"start": v(3.84, 7.1) * mm, "end": v(3.8, 7.34) * mm});
            skArc(sketch, "E13.26.6", {"start": v(3.84, 7.1) * mm, "mid": v(3.84, 7.04) * mm, "end": v(3.83, 6.97) * mm});
            skLineSegment(sketch, "E13.26.7", {"start": v(3.16, 7.43) * mm, "end": v(3.38, 7.54) * mm});
            skArc(sketch, "E13.26.8", {"start": v(3.74, 7.41) * mm, "mid": v(3.77, 7.38) * mm, "end": v(3.8, 7.34) * mm});
            skArc(sketch, "E13.26.9", {"start": v(3.47, 7.54) * mm, "mid": v(3.42, 7.55) * mm, "end": v(3.38, 7.54) * mm});
            skLineSegment(sketch, "E13.26.10", {"start": v(3.6, 7.48) * mm, "end": v(3.74, 7.41) * mm});
            skLineSegment(sketch, "E13.26.11", {"start": v(3.6, 7.48) * mm, "end": v(3.47, 7.54) * mm});
            skLineSegment(sketch, "E13.26.12", {"start": v(3.07, 7.34) * mm, "end": v(2.87, 6.93) * mm});
            skLineSegment(sketch, "E13.26.13", {"start": v(3.83, 6.97) * mm, "end": v(3.63, 6.56) * mm});
            skPoint(sketch, "E13.27.0", {"position": v(1.37, 7.9) * mm});
            skPoint(sketch, "E13.27.1", {"position": v(2.04, 8.05) * mm});
            skPoint(sketch, "E13.27.2", {"position": v(2.2, 7.72) * mm});
            skPoint(sketch, "E13.27.3", {"position": v(1.65, 8.14) * mm});
            skArc(sketch, "E13.27.4", {"start": v(1.43, 7.95) * mm, "mid": v(1.38, 7.9) * mm, "end": v(1.36, 7.84) * mm});
            skLineSegment(sketch, "E13.27.5", {"start": v(2.16, 7.78) * mm, "end": v(2.06, 8) * mm});
            skArc(sketch, "E13.27.6", {"start": v(2.16, 7.78) * mm, "mid": v(2.18, 7.72) * mm, "end": v(2.18, 7.65) * mm});
            skLineSegment(sketch, "E13.27.7", {"start": v(1.43, 7.95) * mm, "end": v(1.61, 8.1) * mm});
            skArc(sketch, "E13.27.8", {"start": v(2, 8.06) * mm, "mid": v(2.03, 8.04) * mm, "end": v(2.06, 8) * mm});
            skArc(sketch, "E13.27.9", {"start": v(1.7, 8.13) * mm, "mid": v(1.66, 8.13) * mm, "end": v(1.61, 8.1) * mm});
            skLineSegment(sketch, "E13.27.10", {"start": v(1.85, 8.1) * mm, "end": v(2, 8.06) * mm});
            skLineSegment(sketch, "E13.27.11", {"start": v(1.85, 8.1) * mm, "end": v(1.7, 8.13) * mm});
            skLineSegment(sketch, "E13.27.12", {"start": v(1.36, 7.84) * mm, "end": v(1.26, 7.4) * mm});
            skLineSegment(sketch, "E13.27.13", {"start": v(2.18, 7.65) * mm, "end": v(2.08, 7.2) * mm});
            skCircle(sketch, "E14", {"center": v(0, 0) * mm, "radius": 5 * mm});
            skSolve(sketch);
        }
        {
            var Q0;
            Q0=makeQuery(id+"F0.imprint","IMPRINT",FACE,{"disambiguationData":[TD([[makeQuery(id+"F0.imprint","IMPRINT",EDGE,{"derivedFrom":sQuery(id+"F0.wireOp",EDGE,"E13.22.4")}),1.0]])]});
            var Q1;
            Q1=makeQuery(id+"F0.imprint","IMPRINT",FACE,{"disambiguationData":[TD([[makeQuery(id+"F0.imprint","IMPRINT",EDGE,{"derivedFrom":sQuery(id+"F0.wireOp",EDGE,"E13.23.4")}),1.0]])]});
            var Q2;
            Q2=makeQuery(id+"F0.imprint","IMPRINT",FACE,{"disambiguationData":[TD([[makeQuery(id+"F0.imprint","IMPRINT",EDGE,{"derivedFrom":sQuery(id+"F0.wireOp",EDGE,"E13.24.4")}),1.0]])]});
            var Q3;
            Q3=makeQuery(id+"F0.imprint","IMPRINT",FACE,{"disambiguationData":[TD([[makeQuery(id+"F0.imprint","IMPRINT",EDGE,{"derivedFrom":sQuery(id+"F0.wireOp",EDGE,"E13.25.4")}),1.0]])]});
            var Q4;
            Q4=makeQuery(id+"F0.imprint","IMPRINT",FACE,{"disambiguationData":[TD([[makeQuery(id+"F0.imprint","IMPRINT",EDGE,{"derivedFrom":sQuery(id+"F0.wireOp",EDGE,"E13.26.4")}),1.0]])]});
            var Q5;
            Q5=makeQuery(id+"F0.imprint","IMPRINT",FACE,{"disambiguationData":[TD([[makeQuery(id+"F0.imprint","IMPRINT",EDGE,{"derivedFrom":sQuery(id+"F0.wireOp",EDGE,"E13.27.4")}),1.0]])]});
            var Q6;
            Q6=makeQuery(id+"F0.imprint","IMPRINT",FACE,{"disambiguationData":[TD([[makeQuery(id+"F0.imprint","IMPRINT",EDGE,{"derivedFrom":sQuery(id+"F0.wireOp",EDGE,"E13.1.4")}),1.0]])]});
            var Q7;
            Q7=makeQuery(id+"F0.imprint","IMPRINT",FACE,{"disambiguationData":[TD([[makeQuery(id+"F0.imprint","IMPRINT",EDGE,{"derivedFrom":sQuery(id+"F0.wireOp",EDGE,"E13.2.4")}),1.0]])]});
            var Q8;
            Q8=makeQuery(id+"F0.imprint","IMPRINT",FACE,{"disambiguationData":[TD([[makeQuery(id+"F0.imprint","IMPRINT",EDGE,{"derivedFrom":sQuery(id+"F0.wireOp",EDGE,"E13.3.4")}),1.0]])]});
            var Q9;
            Q9=makeQuery(id+"F0.imprint","IMPRINT",FACE,{"disambiguationData":[TD([[makeQuery(id+"F0.imprint","IMPRINT",EDGE,{"derivedFrom":sQuery(id+"F0.wireOp",EDGE,"E13.4.4")}),1.0]])]});
            var Q10;
            Q10=makeQuery(id+"F0.imprint","IMPRINT",FACE,{"disambiguationData":[TD([[makeQuery(id+"F0.imprint","IMPRINT",EDGE,{"derivedFrom":sQuery(id+"F0.wireOp",EDGE,"E13.5.4")}),1.0]])]});
            var Q11;
            Q11=makeQuery(id+"F0.imprint","IMPRINT",FACE,{"disambiguationData":[TD([[makeQuery(id+"F0.imprint","IMPRINT",EDGE,{"derivedFrom":sQuery(id+"F0.wireOp",EDGE,"E13.6.4")}),1.0]])]});
            var Q12;
            Q12=makeQuery(id+"F0.imprint","IMPRINT",FACE,{"disambiguationData":[TD([[makeQuery(id+"F0.imprint","IMPRINT",EDGE,{"derivedFrom":sQuery(id+"F0.wireOp",EDGE,"E13.7.4")}),1.0]])]});
            var Q13;
            Q13=makeQuery(id+"F0.imprint","IMPRINT",FACE,{"disambiguationData":[TD([[makeQuery(id+"F0.imprint","IMPRINT",EDGE,{"derivedFrom":sQuery(id+"F0.wireOp",EDGE,"E13.8.4")}),1.0]])]});
            var Q14;
            Q14=makeQuery(id+"F0.imprint","IMPRINT",FACE,{"disambiguationData":[TD([[makeQuery(id+"F0.imprint","IMPRINT",EDGE,{"derivedFrom":sQuery(id+"F0.wireOp",EDGE,"E13.9.4")}),1.0]])]});
            var Q15;
            Q15=makeQuery(id+"F0.imprint","IMPRINT",FACE,{"disambiguationData":[TD([[makeQuery(id+"F0.imprint","IMPRINT",EDGE,{"derivedFrom":sQuery(id+"F0.wireOp",EDGE,"E13.10.4")}),1.0]])]});
            var Q16;
            Q16=makeQuery(id+"F0.imprint","IMPRINT",FACE,{"disambiguationData":[TD([[makeQuery(id+"F0.imprint","IMPRINT",EDGE,{"derivedFrom":sQuery(id+"F0.wireOp",EDGE,"E13.11.4")}),1.0]])]});
            var Q17;
            Q17=makeQuery(id+"F0.imprint","IMPRINT",FACE,{"disambiguationData":[TD([[makeQuery(id+"F0.imprint","IMPRINT",EDGE,{"derivedFrom":sQuery(id+"F0.wireOp",EDGE,"E13.12.4")}),1.0]])]});
            var Q18;
            Q18=makeQuery(id+"F0.imprint","IMPRINT",FACE,{"disambiguationData":[TD([[makeQuery(id+"F0.imprint","IMPRINT",EDGE,{"derivedFrom":sQuery(id+"F0.wireOp",EDGE,"E13.13.4")}),1.0]])]});
            var Q19;
            Q19=makeQuery(id+"F0.imprint","IMPRINT",FACE,{"disambiguationData":[TD([[makeQuery(id+"F0.imprint","IMPRINT",EDGE,{"derivedFrom":sQuery(id+"F0.wireOp",EDGE,"E13.14.4")}),1.0]])]});
            var Q20;
            Q20=makeQuery(id+"F0.imprint","IMPRINT",FACE,{"disambiguationData":[TD([[makeQuery(id+"F0.imprint","IMPRINT",EDGE,{"derivedFrom":sQuery(id+"F0.wireOp",EDGE,"E13.15.4")}),1.0]])]});
            var Q21;
            Q21=makeQuery(id+"F0.imprint","IMPRINT",FACE,{"disambiguationData":[TD([[makeQuery(id+"F0.imprint","IMPRINT",EDGE,{"derivedFrom":sQuery(id+"F0.wireOp",EDGE,"E13.16.4")}),1.0]])]});
            var Q22;
            Q22=makeQuery(id+"F0.imprint","IMPRINT",FACE,{"disambiguationData":[TD([[makeQuery(id+"F0.imprint","IMPRINT",EDGE,{"derivedFrom":sQuery(id+"F0.wireOp",EDGE,"E13.17.4")}),1.0]])]});
            var Q23;
            Q23=makeQuery(id+"F0.imprint","IMPRINT",FACE,{"disambiguationData":[TD([[makeQuery(id+"F0.imprint","IMPRINT",EDGE,{"derivedFrom":sQuery(id+"F0.wireOp",EDGE,"E13.18.4")}),1.0]])]});
            var Q24;
            Q24=makeQuery(id+"F0.imprint","IMPRINT",FACE,{"disambiguationData":[TD([[makeQuery(id+"F0.imprint","IMPRINT",EDGE,{"derivedFrom":sQuery(id+"F0.wireOp",EDGE,"E13.19.4")}),1.0]])]});
            var Q25;
            Q25=makeQuery(id+"F0.imprint","IMPRINT",FACE,{"disambiguationData":[TD([[makeQuery(id+"F0.imprint","IMPRINT",EDGE,{"derivedFrom":sQuery(id+"F0.wireOp",EDGE,"E13.20.4")}),1.0]])]});
            var Q26;
            Q26=makeQuery(id+"F0.imprint","IMPRINT",FACE,{"disambiguationData":[TD([[makeQuery(id+"F0.imprint","IMPRINT",EDGE,{"derivedFrom":sQuery(id+"F0.wireOp",EDGE,"E13.21.4")}),1.0]])]});
            var Q27;
            {var subQ0=sQuery(id+"F0.wireOp",EDGE,"E1.left");Q27=makeQuery(id+"F0.imprint","IMPRINT",FACE,{"disambiguationData":[TD([[makeQuery(id+"F0.imprint","IMPRINT",EDGE,{"derivedFrom":subQ0}),1.0]])]});}
            var Q28;
            Q28=makeQuery(id+"F0.imprint","IMPRINT",FACE,{"disambiguationData":[TD([[makeQuery(id+"F0.imprint","IMPRINT",EDGE,{"derivedFrom":sQuery(id+"F0.wireOp",EDGE,"E1.bottom")}),1.0]])]});
            var Q29;
            Q29=makeQuery(id+"F0.imprint","IMPRINT",FACE,{"disambiguationData":[TD([[makeQuery(id+"F0.imprint","IMPRINT",EDGE,{"derivedFrom":sQuery(id+"F0.wireOp",EDGE,"E14")}),-1.0]])]});
            extrude(context, id + "F1", {"entities" : qUnion([Q0, Q1, Q2, Q3, Q4, Q5, Q6, Q7, Q8, Q9, Q10, Q11, Q12, Q13, Q14, Q15, Q16, Q17, Q18, Q19, Q20, Q21, Q22, Q23, Q24, Q25, Q26, Q27, Q28, Q29]), "endBound" : BoundingType.SYMMETRIC, "depth" : 5 * mm});
        }
    });
